# Revit family: ITK_Проходной адаптер категории 5E_Keystone Jack_Экранированный
name_source: partatom
category: Обобщенные модели
units: mm (PartAtom-declared; Revit-internal decimal feet)

## family parameters
Всегда вертикально = Да
Может служить основой для арматурных стержней = Нет
На основе рабочей плоскости = Нет
Общий = Нет
При загрузке вырезать с полостями = Нет
Размер круглого соединителя = Использовать диаметр
Тип детали = Нормальный
Точка расчета площади = Нет

## types (1)
- CS7-1C5EF
    ADSK_URL страницы изделия = https://www.itk-group.ru
    ADSK_Версия Revit = 2019
    ADSK_Версия семейства = 1.0
    ADSK_Группирование = I. ЩИТЫ И ПУЛЬТЫ
    ADSK_Единица измерения = шт
    ADSK_Завод-изготовитель = IEK
    ADSK_Код изделия = CS7-1C5EF
    ADSK_Масса = 0
    ADSK_Материал наименование = Металл и АБС-пластик
    ADSK_Наименование = IITK Проходной адаптер кат. 5E FTP RJ45-RJ45 Keystone Jack
    IEK_URL = https://www.itk-group.ru
    IEK_Описание = Соответствие международным стандартам качества, что обеспечивает совместимость с компонентами и с кабелем.
Изготовлены из высококачественных негорючих материалов и отличаются надежностью и удобством эксплуатации.
    IEK_Цена за единицу = 229.49
    KSI_CMa_Строительные материалы = 10.3.02.06
    KSI_CPr_Строительные изделия = 61.1.03.04
    URL = https://www.iek.ru
    Высота = 16 мм
    Глубина = 33 мм
    Изготовитель = ITK
    Материал = Нержавеющая сталь
    Ширина = 15 мм
